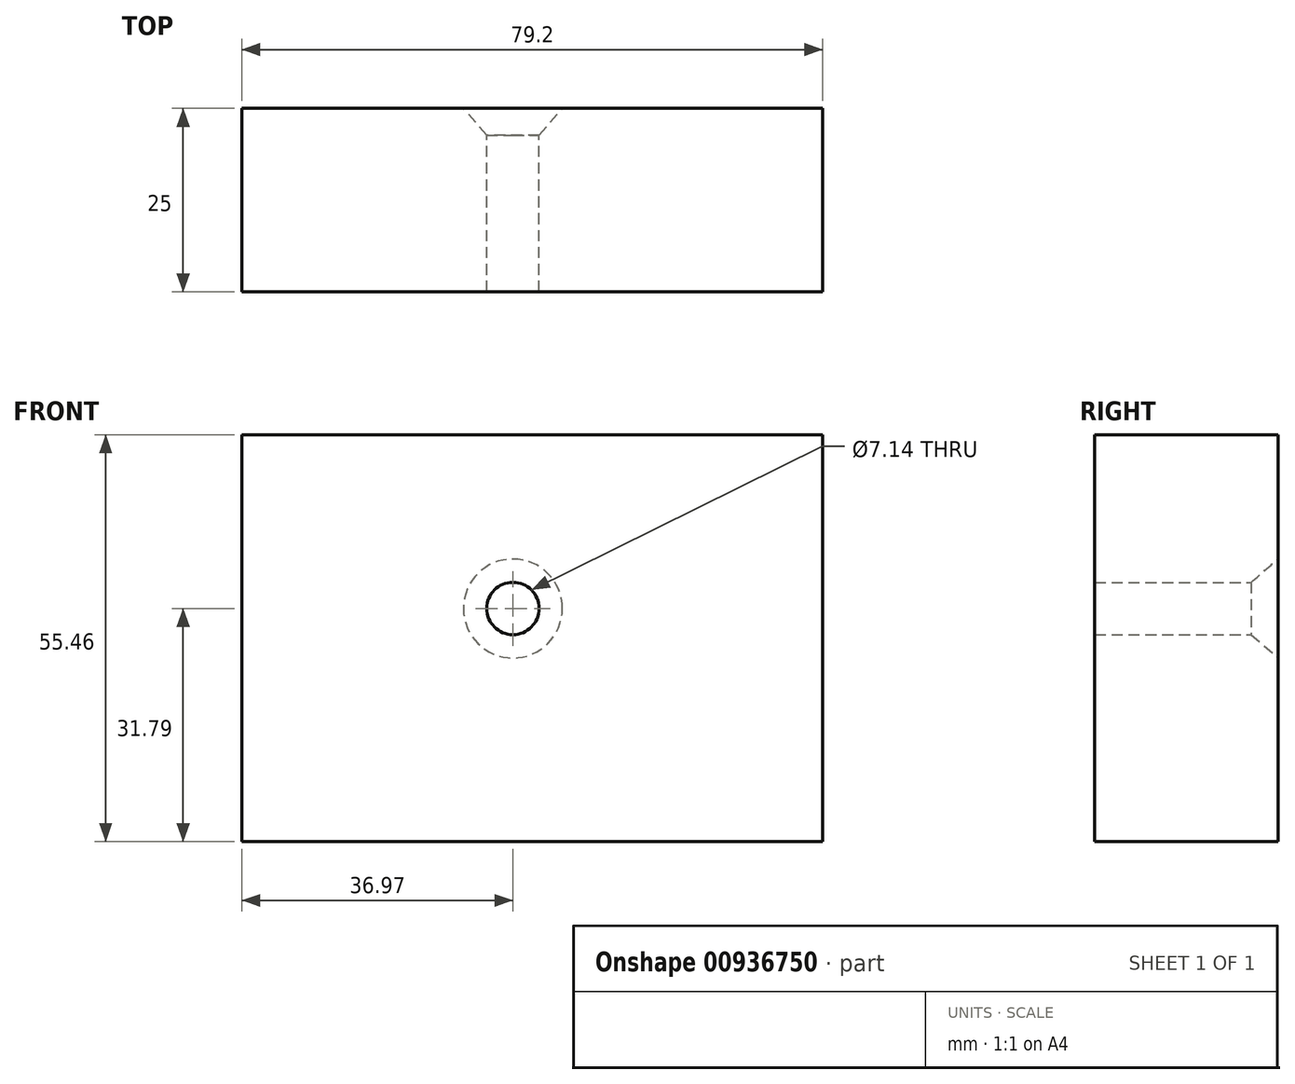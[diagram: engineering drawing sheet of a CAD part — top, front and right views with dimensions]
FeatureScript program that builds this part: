
annotation { "Feature Type Name" : "Feature", "Feature Type Description" : "" }
export const myFeature = defineFeature(function(context is Context, id is Id, definition is map)
    precondition{}
    {
        {
            var Q0;
            Q0=qCreatedBy(makeId("Front.planeOp"),FACE);
            var sketch = newSketch(context, id + "F0", { "sketchPlane" : qUnion([Q0])});
            skPoint(sketch, "E0", {"position": v(0, 0) * mm});
            skLineSegment(sketch, "E1.bottom", {"start": v(-36.97, 23.67) * mm, "end": v(42.23, 23.67) * mm});
            skLineSegment(sketch, "E1.top", {"start": v(-36.97, -31.8) * mm, "end": v(42.23, -31.8) * mm});
            skLineSegment(sketch, "E1.left", {"start": v(-36.97, 23.67) * mm, "end": v(-36.97, -31.8) * mm});
            skLineSegment(sketch, "E1.right", {"start": v(42.23, 23.67) * mm, "end": v(42.23, -31.8) * mm});
            skSolve(sketch);
        }
        {
            var Q0;
            Q0 = qSketchRegion(id + "F0", true);
            extrude(context, id + "F1", {"entities" : qUnion([Q0]), "depth" : 25 * mm, "offsetDistance" : 25 * mm});
        }
        {
            var Q0;
            Q0=sQuery(id+"F0.wireOp",VERTEX,"E0");
            var Q1;
            Q1=makeQuery(id+"F1.opExtrude","SWEPT_BODY",BODY,{"disambiguationData":[OSD([sQuery(id+"F0.wireOp",EDGE,"E1.bottom"),sQuery(id+"F0.wireOp",EDGE,"E1.top"),sQuery(id+"F0.wireOp",EDGE,"E1.left"),sQuery(id+"F0.wireOp",EDGE,"E1.right")])]});
            hole(context, id + "F2", {"style" : HoleStyle.C_SINK, "endStyle" : HoleEndStyle.THROUGH, "oppositeDirection" : true, "standardTappedOrClearance" : lookupTablePath({ "fit" : "Normal (ASME)", "standard" : "ANSI", "size" : "1/4", "type" : "Clearance" }), "standardBlindInLast" : lookupTablePath({ "fit" : "Normal", "standard" : "ANSI", "engagement" : "75%", "pitch" : "20 tpi", "size" : "1/4", "type" : "Clearance & tapped" }), "holeDiameter" : 7.14 * mm, "cSinkDiameter" : 13.5 * mm, "cSinkAngle" : 82 * degree, "majorDiameter" : 5 * mm, "isTappedThrough" : true, "tappedDepth" : 12 * mm, "tapClearance" : 3, "locations" : qUnion([Q0]), "scope" : qUnion([Q1])});
        }
    });
